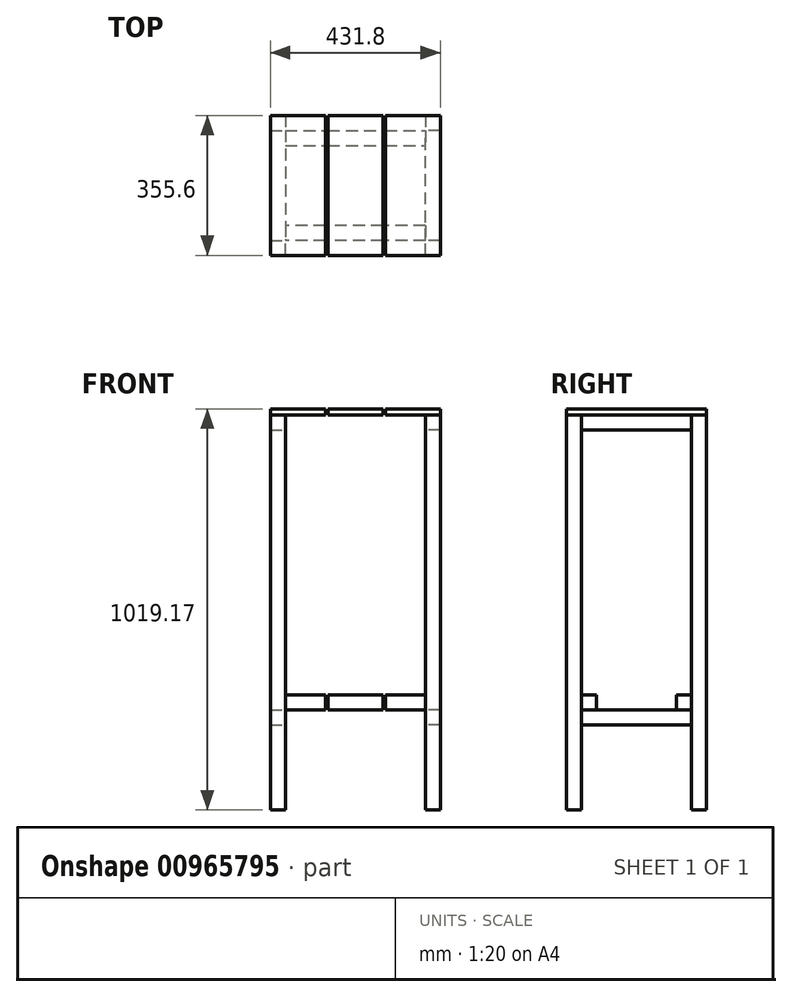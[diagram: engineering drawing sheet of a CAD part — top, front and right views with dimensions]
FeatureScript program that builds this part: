
annotation { "Feature Type Name" : "Feature", "Feature Type Description" : "" }
export const myFeature = defineFeature(function(context is Context, id is Id, definition is map)
    precondition{}
    {
        {
            var Q0;
            Q0=qCreatedBy(makeId("Top.planeOp"),FACE);
            var sketch = newSketch(context, id + "F0", { "sketchPlane" : qUnion([Q0])});
            skLineSegment(sketch, "E0.bottom", {"start": v(215.9, 177.8) * mm, "end": v(-215.9, 177.8) * mm, "construction": true});
            skLineSegment(sketch, "E0.top", {"start": v(215.9, -177.8) * mm, "end": v(-215.9, -177.8) * mm, "construction": true});
            skLineSegment(sketch, "E0.left", {"start": v(215.9, 177.8) * mm, "end": v(215.9, -177.8) * mm, "construction": true});
            skLineSegment(sketch, "E0.right", {"start": v(-215.9, 177.8) * mm, "end": v(-215.9, -177.8) * mm, "construction": true});
            skPoint(sketch, "E0.middle", {"position": v(0, 0) * mm});
            skLineSegment(sketch, "E1.bottom", {"start": v(-215.9, 177.8) * mm, "end": v(-177.8, 177.8) * mm});
            skLineSegment(sketch, "E1.top", {"start": v(-215.9, 139.7) * mm, "end": v(-177.8, 139.7) * mm});
            skLineSegment(sketch, "E1.left", {"start": v(-215.9, 177.8) * mm, "end": v(-215.9, 139.7) * mm});
            skLineSegment(sketch, "E1.right", {"start": v(-177.8, 177.8) * mm, "end": v(-177.8, 139.7) * mm});
            skLineSegment(sketch, "E2.bottom", {"start": v(215.9, 177.8) * mm, "end": v(177.8, 177.8) * mm});
            skLineSegment(sketch, "E2.top", {"start": v(215.9, 139.7) * mm, "end": v(177.8, 139.7) * mm});
            skLineSegment(sketch, "E2.left", {"start": v(215.9, 177.8) * mm, "end": v(215.9, 139.7) * mm});
            skLineSegment(sketch, "E2.right", {"start": v(177.8, 177.8) * mm, "end": v(177.8, 139.7) * mm});
            skLineSegment(sketch, "E3.bottom", {"start": v(215.9, -177.8) * mm, "end": v(177.8, -177.8) * mm});
            skLineSegment(sketch, "E3.top", {"start": v(215.9, -139.7) * mm, "end": v(177.8, -139.7) * mm});
            skLineSegment(sketch, "E3.left", {"start": v(215.9, -177.8) * mm, "end": v(215.9, -139.7) * mm});
            skLineSegment(sketch, "E3.right", {"start": v(177.8, -177.8) * mm, "end": v(177.8, -139.7) * mm});
            skLineSegment(sketch, "E4.bottom", {"start": v(-215.9, -177.8) * mm, "end": v(-177.8, -177.8) * mm});
            skLineSegment(sketch, "E4.top", {"start": v(-215.9, -139.7) * mm, "end": v(-177.8, -139.7) * mm});
            skLineSegment(sketch, "E4.left", {"start": v(-215.9, -177.8) * mm, "end": v(-215.9, -139.7) * mm});
            skLineSegment(sketch, "E4.right", {"start": v(-177.8, -177.8) * mm, "end": v(-177.8, -139.7) * mm});
            skSolve(sketch);
        }
        {
            var Q0;
            Q0=makeQuery(id+"F0.imprint","IMPRINT",FACE,{"disambiguationData":[TD([[makeQuery(id+"F0.imprint","IMPRINT",EDGE,{"derivedFrom":sQuery(id+"F0.wireOp",EDGE,"E1.bottom")}),-1.0]])]});
            var Q1;
            Q1=makeQuery(id+"F0.imprint","IMPRINT",FACE,{"disambiguationData":[TD([[makeQuery(id+"F0.imprint","IMPRINT",EDGE,{"derivedFrom":sQuery(id+"F0.wireOp",EDGE,"E4.bottom")}),1.0]])]});
            var Q2;
            Q2=makeQuery(id+"F0.imprint","IMPRINT",FACE,{"disambiguationData":[TD([[makeQuery(id+"F0.imprint","IMPRINT",EDGE,{"derivedFrom":sQuery(id+"F0.wireOp",EDGE,"E3.bottom")}),-1.0]])]});
            var Q3;
            Q3=makeQuery(id+"F0.imprint","IMPRINT",FACE,{"disambiguationData":[TD([[makeQuery(id+"F0.imprint","IMPRINT",EDGE,{"derivedFrom":sQuery(id+"F0.wireOp",EDGE,"E2.bottom")}),1.0]])]});
            extrude(context, id + "F1", {"entities" : qUnion([Q0, Q1, Q2, Q3]), "depth" : 1003.3 * mm, "offsetDistance" : 25.4 * mm});
        }
        {
            var Q0;
            Q0=makeQuery(id+"F1.opExtrude","CAP_FACE",FACE,{"disambiguationData":[OSD([sQuery(id+"F0.wireOp",EDGE,"E4.bottom"),sQuery(id+"F0.wireOp",EDGE,"E4.top"),sQuery(id+"F0.wireOp",EDGE,"E4.left"),sQuery(id+"F0.wireOp",EDGE,"E4.right")])],"isStart":false});
            var sketch = newSketch(context, id + "F2", { "sketchPlane" : qUnion([Q0])});
            skLineSegment(sketch, "E5.bottom", {"start": v(215.9, 177.8) * mm, "end": v(-215.9, 177.8) * mm});
            skLineSegment(sketch, "E5.top", {"start": v(215.9, -177.8) * mm, "end": v(-215.9, -177.8) * mm});
            skLineSegment(sketch, "E5.left", {"start": v(215.9, 177.8) * mm, "end": v(215.9, -177.8) * mm});
            skLineSegment(sketch, "E5.right", {"start": v(-215.9, 177.8) * mm, "end": v(-215.9, -177.8) * mm});
            skPoint(sketch, "E5.middle", {"position": v(0, 0) * mm});
            skSolve(sketch);
        }
        {
            var Q0;
            Q0=makeQuery(id+"F2.imprint","IMPRINT",FACE,{"disambiguationData":[TD([[makeQuery(id+"F2.imprint","IMPRINT",EDGE,{"derivedFrom":sQuery(id+"F2.wireOp",EDGE,"E5.bottom")}),1.0]])]});
            var Q1;
            Q1=makeQuery(id+"F2.imprint","IMPRINT",FACE,{"disambiguationData":[TD([[makeQuery(id+"F2.imprint","IMPRINT",EDGE,{"derivedFrom":makeQuery(id+"F1.opExtrude","CAP_EDGE",EDGE,{"disambiguationData":[OSD([sQuery(id+"F0.wireOp",EDGE,"E4.bottom")])],"isStart":false})}),1.0]])]});
            var Q2;
            {var subQ4=makeQuery(id+"F1.opExtrude","CAP_EDGE",EDGE,{"disambiguationData":[OSD([sQuery(id+"F0.wireOp",EDGE,"E4.top")])],"isStart":false});Q2=makeQuery(id+"F2.imprint","IMPRINT",FACE,{"disambiguationData":[TD([[makeQuery(id+"F2.imprint","IMPRINT",EDGE,{"derivedFrom":subQ4}),-1.0]])]});}
            extrude(context, id + "F3", {"entities" : qUnion([Q0, Q1, Q2]), "depth" : 15.88 * mm, "offsetDistance" : 25.4 * mm});
        }
        {
            var Q0;
            Q0=makeQuery(id+"F3.opExtrude","CAP_FACE",FACE,{"disambiguationData":[OSD([sQuery(id+"F2.wireOp",EDGE,"E5.bottom"),sQuery(id+"F2.wireOp",EDGE,"E5.top"),sQuery(id+"F2.wireOp",EDGE,"E5.left"),sQuery(id+"F2.wireOp",EDGE,"E5.right")])],"isStart":true});
            var sketch = newSketch(context, id + "F4", { "sketchPlane" : qUnion([Q0])});
            skLineSegment(sketch, "E6.bottom", {"start": v(-215.9, 177.8) * mm, "end": v(215.9, 177.8) * mm});
            skLineSegment(sketch, "E6.top", {"start": v(-215.9, 177.8) * mm, "end": v(215.9, 177.8) * mm});
            skLineSegment(sketch, "E6.left", {"start": v(-215.9, 177.8) * mm, "end": v(-215.9, 177.8) * mm});
            skLineSegment(sketch, "E6.right", {"start": v(215.9, 177.8) * mm, "end": v(215.9, 177.8) * mm});
            skLineSegment(sketch, "E7.bottom", {"start": v(215.9, -177.8) * mm, "end": v(-215.9, -177.8) * mm});
            skLineSegment(sketch, "E7.top", {"start": v(215.9, -177.8) * mm, "end": v(-215.9, -177.8) * mm});
            skLineSegment(sketch, "E7.left", {"start": v(215.9, -177.8) * mm, "end": v(215.9, -177.8) * mm});
            skLineSegment(sketch, "E7.right", {"start": v(-215.9, -177.8) * mm, "end": v(-215.9, -177.8) * mm});
            skLineSegment(sketch, "E8.left", {"start": v(-215.9, -177.8) * mm, "end": v(-215.9, 177.8) * mm});
            skLineSegment(sketch, "E8.right", {"start": v(-215.9, -177.8) * mm, "end": v(-215.9, 177.8) * mm});
            skLineSegment(sketch, "E9.left", {"start": v(215.9, 177.8) * mm, "end": v(215.9, -177.8) * mm});
            skLineSegment(sketch, "E9.right", {"start": v(215.9, 177.8) * mm, "end": v(215.9, -177.8) * mm});
            skLineSegment(sketch, "E10.bottom", {"start": v(-177.8, 177.8) * mm, "end": v(177.8, 177.8) * mm});
            skLineSegment(sketch, "E10.top", {"start": v(-177.8, 139.7) * mm, "end": v(177.8, 139.7) * mm});
            skLineSegment(sketch, "E10.left", {"start": v(-177.8, 177.8) * mm, "end": v(-177.8, 139.7) * mm});
            skLineSegment(sketch, "E10.right", {"start": v(177.8, 177.8) * mm, "end": v(177.8, 139.7) * mm});
            skLineSegment(sketch, "E11.bottom", {"start": v(215.9, 139.7) * mm, "end": v(177.8, 139.7) * mm});
            skLineSegment(sketch, "E11.top", {"start": v(215.9, -139.7) * mm, "end": v(177.8, -139.7) * mm});
            skLineSegment(sketch, "E11.left", {"start": v(215.9, 139.7) * mm, "end": v(215.9, -139.7) * mm});
            skLineSegment(sketch, "E11.right", {"start": v(177.8, 139.7) * mm, "end": v(177.8, -139.7) * mm});
            skLineSegment(sketch, "E12.bottom", {"start": v(177.8, -177.8) * mm, "end": v(-177.8, -177.8) * mm});
            skLineSegment(sketch, "E12.top", {"start": v(177.8, -139.7) * mm, "end": v(-177.8, -139.7) * mm});
            skLineSegment(sketch, "E12.left", {"start": v(177.8, -177.8) * mm, "end": v(177.8, -139.7) * mm});
            skLineSegment(sketch, "E12.right", {"start": v(-177.8, -177.8) * mm, "end": v(-177.8, -139.7) * mm});
            skLineSegment(sketch, "E13.bottom", {"start": v(-215.9, -139.7) * mm, "end": v(-177.8, -139.7) * mm});
            skLineSegment(sketch, "E13.top", {"start": v(-215.9, 139.7) * mm, "end": v(-177.8, 139.7) * mm});
            skLineSegment(sketch, "E13.left", {"start": v(-215.9, -139.7) * mm, "end": v(-215.9, 139.7) * mm});
            skLineSegment(sketch, "E13.right", {"start": v(-177.8, -139.7) * mm, "end": v(-177.8, 139.7) * mm});
            skSolve(sketch);
        }
        {
            var Q0;
            Q0=makeQuery(id+"F4.imprint","IMPRINT",FACE,{"disambiguationData":[TD([[makeQuery(id+"F4.imprint","IMPRINT",EDGE,{"derivedFrom":sQuery(id+"F4.wireOp",EDGE,"E10.bottom")}),1.0]])]});
            var Q1;
            Q1=makeQuery(id+"F4.imprint","IMPRINT",FACE,{"disambiguationData":[TD([[makeQuery(id+"F4.imprint","IMPRINT",EDGE,{"derivedFrom":sQuery(id+"F4.wireOp",EDGE,"E12.bottom")}),-1.0]])]});
            var Q2;
            Q2=makeQuery(id+"F4.imprint","IMPRINT",FACE,{"disambiguationData":[TD([[makeQuery(id+"F4.imprint","IMPRINT",EDGE,{"derivedFrom":sQuery(id+"F4.wireOp",EDGE,"E13.bottom")}),1.0]])]});
            var Q3;
            Q3=makeQuery(id+"F4.imprint","IMPRINT",FACE,{"disambiguationData":[TD([[makeQuery(id+"F4.imprint","IMPRINT",EDGE,{"derivedFrom":sQuery(id+"F4.wireOp",EDGE,"E11.bottom")}),1.0]])]});
            extrude(context, id + "F5", {"entities" : qUnion([Q0, Q1, Q2, Q3]), "depth" : 38.1 * mm, "offsetDistance" : 25.4 * mm});
        }
        {
            var Q0;
            Q0=makeQuery(id+"F1.opExtrude","CAP_FACE",FACE,{"disambiguationData":[OSD([sQuery(id+"F0.wireOp",EDGE,"E1.bottom"),sQuery(id+"F0.wireOp",EDGE,"E1.top"),sQuery(id+"F0.wireOp",EDGE,"E1.left"),sQuery(id+"F0.wireOp",EDGE,"E1.right")])],"isStart":true});
            cPlane(context, id + "F6", {"entities" : qUnion([Q0]), "cplaneType" : CPlaneType.OFFSET, "offset" : 254 * mm, "oppositeDirection" : true, "width" : 152.4 * mm, "height" : 152.4 * mm});
        }
        {
            var Q0;
            Q0=qCreatedBy(id+"F6.planeOp",FACE);
            var sketch = newSketch(context, id + "F7", { "sketchPlane" : qUnion([Q0])});
            skLineSegment(sketch, "E14.bottom", {"start": v(215.9, -139.7) * mm, "end": v(177.8, -139.7) * mm});
            skLineSegment(sketch, "E14.top", {"start": v(215.9, 139.7) * mm, "end": v(177.8, 139.7) * mm});
            skLineSegment(sketch, "E14.left", {"start": v(215.9, -139.7) * mm, "end": v(215.9, 139.7) * mm});
            skLineSegment(sketch, "E14.right", {"start": v(177.8, -139.7) * mm, "end": v(177.8, 139.7) * mm});
            skLineSegment(sketch, "E15.bottom", {"start": v(-215.9, -139.7) * mm, "end": v(-177.8, -139.7) * mm});
            skLineSegment(sketch, "E15.top", {"start": v(-215.9, 139.7) * mm, "end": v(-177.8, 139.7) * mm});
            skLineSegment(sketch, "E15.left", {"start": v(-215.9, -139.7) * mm, "end": v(-215.9, 139.7) * mm});
            skLineSegment(sketch, "E15.right", {"start": v(-177.8, -139.7) * mm, "end": v(-177.8, 139.7) * mm});
            skLineSegment(sketch, "E16.bottom", {"start": v(215.9, 139.7) * mm, "end": v(-215.9, 139.7) * mm});
            skLineSegment(sketch, "E16.top", {"start": v(215.9, 101.6) * mm, "end": v(-215.9, 101.6) * mm});
            skLineSegment(sketch, "E16.left", {"start": v(215.9, 139.7) * mm, "end": v(215.9, 101.6) * mm});
            skLineSegment(sketch, "E16.right", {"start": v(-215.9, 139.7) * mm, "end": v(-215.9, 101.6) * mm});
            skLineSegment(sketch, "E17.bottom", {"start": v(-215.9, -139.7) * mm, "end": v(215.9, -139.7) * mm});
            skLineSegment(sketch, "E17.top", {"start": v(-215.9, -101.6) * mm, "end": v(215.9, -101.6) * mm});
            skLineSegment(sketch, "E17.left", {"start": v(-215.9, -139.7) * mm, "end": v(-215.9, -101.6) * mm});
            skLineSegment(sketch, "E17.right", {"start": v(215.9, -139.7) * mm, "end": v(215.9, -101.6) * mm});
            skSolve(sketch);
        }
        {
            var Q0;
            {var subQ0=sQuery(id+"F7.wireOp",EDGE,"E14.left");Q0=makeQuery(id+"F7.imprint","IMPRINT",FACE,{"disambiguationData":[TD([[makeQuery(id+"F7.imprint","IMPRINT",EDGE,{"derivedFrom":subQ0}),1.0]])]});}
            var Q1;
            {var subQ5=sQuery(id+"F7.wireOp",EDGE,"E17.right");Q1=makeQuery(id+"F7.imprint","IMPRINT",FACE,{"disambiguationData":[TD([[makeQuery(id+"F7.imprint","IMPRINT",EDGE,{"derivedFrom":subQ5}),1.0]])]});}
            var Q2;
            {var subQ5=sQuery(id+"F7.wireOp",EDGE,"E16.left");Q2=makeQuery(id+"F7.imprint","IMPRINT",FACE,{"disambiguationData":[TD([[makeQuery(id+"F7.imprint","IMPRINT",EDGE,{"derivedFrom":subQ5}),-1.0]])]});}
            var Q3;
            {var subQ5=sQuery(id+"F7.wireOp",EDGE,"E16.right");Q3=makeQuery(id+"F7.imprint","IMPRINT",FACE,{"disambiguationData":[TD([[makeQuery(id+"F7.imprint","IMPRINT",EDGE,{"derivedFrom":subQ5}),1.0]])]});}
            var Q4;
            {var subQ0=sQuery(id+"F7.wireOp",EDGE,"E15.left");Q4=makeQuery(id+"F7.imprint","IMPRINT",FACE,{"disambiguationData":[TD([[makeQuery(id+"F7.imprint","IMPRINT",EDGE,{"derivedFrom":subQ0}),-1.0]])]});}
            var Q5;
            {var subQ5=sQuery(id+"F7.wireOp",EDGE,"E17.left");Q5=makeQuery(id+"F7.imprint","IMPRINT",FACE,{"disambiguationData":[TD([[makeQuery(id+"F7.imprint","IMPRINT",EDGE,{"derivedFrom":subQ5}),-1.0]])]});}
            extrude(context, id + "F8", {"entities" : qUnion([Q0, Q1, Q2, Q3, Q4, Q5]), "depth" : 38.1 * mm, "offsetDistance" : 25.4 * mm});
        }
        {
            var Q0;
            {var subQ5=sQuery(id+"F7.wireOp",EDGE,"E16.left");Q0=makeQuery(id+"F7.imprint","IMPRINT",FACE,{"disambiguationData":[TD([[makeQuery(id+"F7.imprint","IMPRINT",EDGE,{"derivedFrom":subQ5}),-1.0]])]});}
            var Q1;
            {var subQ0=sQuery(id+"F7.wireOp",EDGE,"E16.bottom");var subQ1=sQuery(id+"F7.wireOp",EDGE,"E14.right");var subQ2=makeQuery(id+"F7.imprint","INTERSECT",VERTEX,{"derivedFrom":[subQ1,subQ0]});Q1=makeQuery(id+"F7.imprint","IMPRINT",FACE,{"disambiguationData":[TD([[makeQuery(id+"F7.imprint","IMPRINT",EDGE,{"disambiguationData":[TD([[subQ2,1.0]])],"derivedFrom":subQ1}),1.0]])]});}
            var Q2;
            {var subQ5=sQuery(id+"F7.wireOp",EDGE,"E16.right");Q2=makeQuery(id+"F7.imprint","IMPRINT",FACE,{"disambiguationData":[TD([[makeQuery(id+"F7.imprint","IMPRINT",EDGE,{"derivedFrom":subQ5}),1.0]])]});}
            var Q3;
            {var subQ5=sQuery(id+"F7.wireOp",EDGE,"E17.left");Q3=makeQuery(id+"F7.imprint","IMPRINT",FACE,{"disambiguationData":[TD([[makeQuery(id+"F7.imprint","IMPRINT",EDGE,{"derivedFrom":subQ5}),-1.0]])]});}
            var Q4;
            {var subQ0=sQuery(id+"F7.wireOp",EDGE,"E17.bottom");var subQ1=sQuery(id+"F7.wireOp",EDGE,"E14.right");var subQ2=makeQuery(id+"F7.imprint","INTERSECT",VERTEX,{"derivedFrom":[subQ1,subQ0]});Q4=makeQuery(id+"F7.imprint","IMPRINT",FACE,{"disambiguationData":[TD([[makeQuery(id+"F7.imprint","IMPRINT",EDGE,{"disambiguationData":[TD([[subQ2,-1.0]])],"derivedFrom":subQ1}),1.0]])]});}
            var Q5;
            {var subQ5=sQuery(id+"F7.wireOp",EDGE,"E17.right");Q5=makeQuery(id+"F7.imprint","IMPRINT",FACE,{"disambiguationData":[TD([[makeQuery(id+"F7.imprint","IMPRINT",EDGE,{"derivedFrom":subQ5}),1.0]])]});}
            extrude(context, id + "F9", {"entities" : qUnion([Q0, Q1, Q2, Q3, Q4, Q5]), "oppositeDirection" : true, "depth" : 38.1 * mm, "offsetDistance" : 25.4 * mm});
        }
        {
            var Q0;
            Q0=makeQuery(id+"F3.opExtrude","CAP_FACE",FACE,{"disambiguationData":[OSD([sQuery(id+"F2.wireOp",EDGE,"E5.bottom"),sQuery(id+"F2.wireOp",EDGE,"E5.top"),sQuery(id+"F2.wireOp",EDGE,"E5.left"),sQuery(id+"F2.wireOp",EDGE,"E5.right")])],"isStart":false});
            var sketch = newSketch(context, id + "F10", { "sketchPlane" : qUnion([Q0])});
            skLineSegment(sketch, "E18.bottom", {"start": v(-215.9, -177.8) * mm, "end": v(-76.2, -177.8) * mm});
            skLineSegment(sketch, "E18.top", {"start": v(-215.9, 177.8) * mm, "end": v(-76.2, 177.8) * mm});
            skLineSegment(sketch, "E18.left", {"start": v(-215.9, -177.8) * mm, "end": v(-215.9, 177.8) * mm});
            skLineSegment(sketch, "E18.right", {"start": v(-76.2, -177.8) * mm, "end": v(-76.2, 177.8) * mm});
            skLineSegment(sketch, "E19.bottom", {"start": v(215.9, 177.8) * mm, "end": v(76.2, 177.8) * mm});
            skLineSegment(sketch, "E19.top", {"start": v(215.9, -177.8) * mm, "end": v(76.2, -177.8) * mm});
            skLineSegment(sketch, "E19.left", {"start": v(215.9, 177.8) * mm, "end": v(215.9, -177.8) * mm});
            skLineSegment(sketch, "E19.right", {"start": v(76.2, 177.8) * mm, "end": v(76.2, -177.8) * mm});
            skLineSegment(sketch, "E20.bottom", {"start": v(69.85, -177.8) * mm, "end": v(-69.85, -177.8) * mm});
            skLineSegment(sketch, "E20.top", {"start": v(69.85, 177.8) * mm, "end": v(-69.85, 177.8) * mm});
            skLineSegment(sketch, "E20.left", {"start": v(69.85, -177.8) * mm, "end": v(69.85, 177.8) * mm});
            skLineSegment(sketch, "E20.right", {"start": v(-69.85, -177.8) * mm, "end": v(-69.85, 177.8) * mm});
            skLineSegment(sketch, "E21", {"start": v(0, -177.8) * mm, "end": v(0, 177.8) * mm, "construction": true});
            skSolve(sketch);
        }
        {
            var Q0;
            {var subQ0=sQuery(id+"F10.wireOp",EDGE,"E18.right");Q0=makeQuery(id+"F10.imprint","IMPRINT",FACE,{"disambiguationData":[TD([[makeQuery(id+"F10.imprint","IMPRINT",EDGE,{"derivedFrom":subQ0}),-1.0]])]});}
            var Q1;
            {var subQ0=sQuery(id+"F10.wireOp",EDGE,"E19.right");Q1=makeQuery(id+"F10.imprint","IMPRINT",FACE,{"disambiguationData":[TD([[makeQuery(id+"F10.imprint","IMPRINT",EDGE,{"derivedFrom":subQ0}),-1.0]])]});}
            extrude(context, id + "F11", {"entities" : qUnion([Q0, Q1]), "operationType" : NewBodyOperationType.REMOVE, "endBound" : BoundingType.THROUGH_ALL, "oppositeDirection" : true, "depth" : 25.4 * mm, "offsetDistance" : 25.4 * mm});
        }
    });
